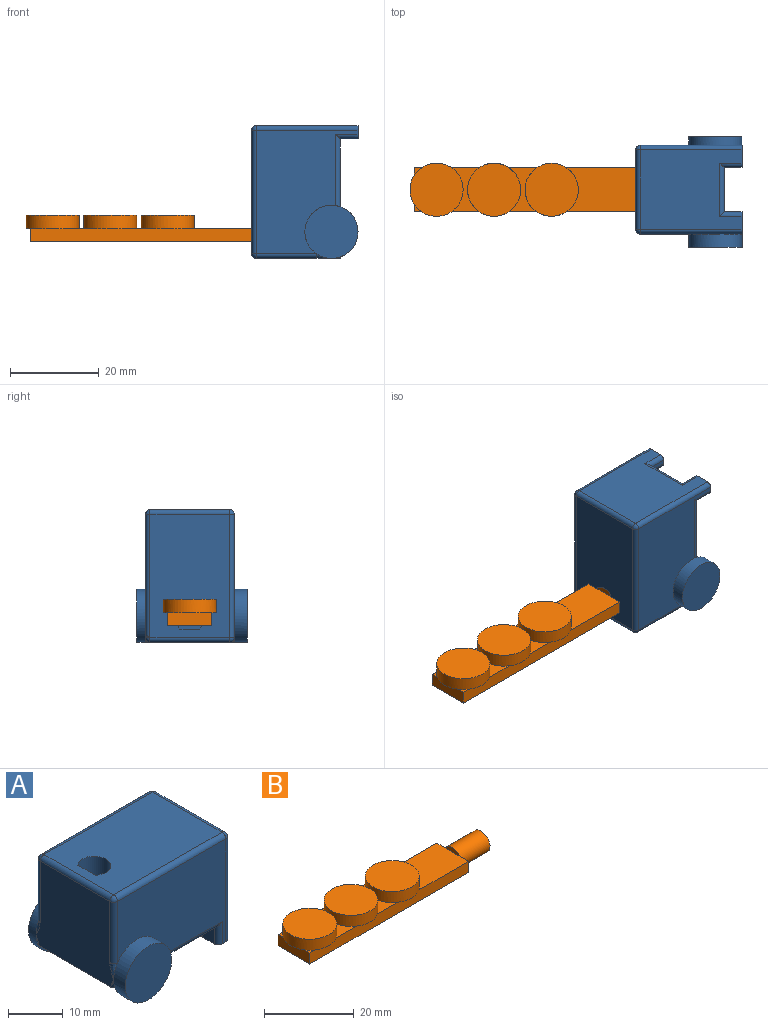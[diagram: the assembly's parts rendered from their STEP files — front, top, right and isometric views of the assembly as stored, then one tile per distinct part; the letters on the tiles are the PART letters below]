
ASSEMBLY  parts=2 mates=1
PART A: 46 faces, bbox 30.5x25.5x24.5 mm
  f0: plane 28x23mm, normal (0,-1,0), area 443.7mm2, adj f9,f20,f30,f31,f33,f36,f37
  f1: plane 28x18mm, normal (0,0,1), area 478.8mm2, adj f6,f7,f37,f38,f42,f43
  f2: plane 23x18mm, normal (1,0,0), area 354mm2, adj f17,f20,f23,f24,f25,f36,f42,f45
  f3: plane 28x23mm, normal (0,1,0), area 443.7mm2, adj f13,f17,f27,f28,f39,f43,f45
  f4: plane 20.48x19.48mm, normal (-1,0,0), area 346.8mm2, adj f5,f21,f22,f32,f33,f35,f38,f39
  f5: plane 29.06x20.06mm, normal (0,0,-1), area 529.6mm2, adj f4,f9,f11,f12,f13,f15,f16,f18
  f6: plane 10x4.47mm, normal (1,0,0), area 44.7mm2, adj f1,f7,f8
  f7: cylinder r=3mm len=10mm, axis (0,0,1), area 138mm2, adj f1,f6,f8
  f8: plane 6x5mm, normal (0,0,1), area 25.2mm2, adj f6,f7
  f9: cylinder r=6mm len=12mm, axis (0,1,0), area 113.6mm2, adj f0,f5,f10,f11,f22,f30,f32
  f10: plane 12x12mm, normal (0,-1,0), area 113.1mm2, adj f9
  f11: plane 11.31x4mm, normal (0,1,0), area 33mm2, adj f5,f9
  f12: plane 11.31x4mm, normal (0,-1,0), area 33mm2, adj f5,f13
  f13: cylinder r=6mm len=12mm, axis (0,-1,0), area 75.9mm2, adj f3,f5,f12,f14,f21,f27,f35
  f14: plane 12x12mm, normal (0,1,0), area 113.1mm2, adj f13
  f15: plane 4x1mm, normal (0,-1,0), area 4mm2, adj f5,f17,f25,f26
  f16: plane 4x3mm, normal (-1,0,0), area 12mm2, adj f5,f17,f26,f28
  f17: plane 5x3mm, normal (0,0,-1), area 14.1mm2, adj f2,f3,f15,f16,f25,f26,f28,f45
  f18: plane 4x3mm, normal (-1,0,0), area 12mm2, adj f5,f20,f29,f31
  f19: plane 4x1mm, normal (0,1,0), area 4mm2, adj f5,f20,f23,f29
  f20: plane 5x3mm, normal (0,0,-1), area 14.1mm2, adj f0,f2,f18,f19,f23,f29,f31,f36
  f21: bspline ~2.57x0.89mm, area 0.6mm2, adj f4,f5,f13
  f22: bspline ~2.57x0.89mm, area 0.6mm2, adj f4,f5,f9
  f23: cylinder r=1mm len=5mm, axis (0,0,1), area 7.1mm2, adj f2,f19,f20,f24
  f24: cylinder r=1mm len=12mm, axis (0,1,0), area 17.3mm2, adj f2,f5,f23,f25
  f25: cylinder r=1mm len=5mm, axis (0,0,-1), area 7.1mm2, adj f2,f15,f17,f24
  f26: cylinder r=1mm len=4mm, axis (0,0,-1), area 6.3mm2, adj f5,f15,f16,f17
  f27: cylinder r=1mm len=16.34mm, axis (-1,0,0), area 24.7mm2, adj f3,f5,f13,f28
  f28: cylinder r=1mm len=5mm, axis (0,0,-1), area 7.1mm2, adj f3,f16,f17,f27
  f29: cylinder r=1mm len=4mm, axis (0,0,-1), area 6.3mm2, adj f5,f18,f19,f20
  f30: cylinder r=1mm len=16.34mm, axis (1,0,0), area 24.7mm2, adj f0,f5,f9,f31
  f31: cylinder r=1mm len=5mm, axis (0,0,-1), area 7.1mm2, adj f0,f18,f20,f30
  f32: bspline ~3.69x1.19mm, area 1.6mm2, adj f4,f9,f33
  f33: cylinder r=1mm len=13.68mm, axis (0,0,1), area 21.5mm2, adj f0,f4,f32,f34
  f34: sphere r=1mm, area 1.6mm2, adj f33,f37,f38
  f35: bspline ~3.69x1.19mm, area 1.6mm2, adj f4,f13,f39
  f36: cylinder r=1mm len=23mm, axis (0,0,-1), area 36.1mm2, adj f0,f2,f20,f40
  f37: cylinder r=1mm len=28mm, axis (-1,0,0), area 44mm2, adj f0,f1,f34,f40
  f38: cylinder r=1mm len=18mm, axis (0,1,0), area 28.3mm2, adj f1,f4,f34,f41
  f39: cylinder r=1mm len=13.68mm, axis (0,0,-1), area 21.5mm2, adj f3,f4,f35,f41
  f40: sphere r=1mm, area 1.6mm2, adj f36,f37,f42
  f41: sphere r=1mm, area 2.1mm2, adj f38,f39,f43
  f42: cylinder r=1mm len=18mm, axis (0,-1,0), area 28.3mm2, adj f1,f2,f40,f44
  f43: cylinder r=1mm len=28mm, axis (1,0,0), area 44mm2, adj f1,f3,f41,f44
  f44: sphere r=1mm, area 1mm2, adj f42,f43,f45
  f45: cylinder r=1mm len=23mm, axis (0,0,1), area 36.1mm2, adj f2,f3,f17,f44
PART B: 27 faces, bbox 60x12x6 mm
  f0: plane 3x2.7mm, normal (1,0,0), area 7.2mm2, adj f2,f7,f10,f25
  f1: plane 10x6.37mm, normal (0,0,1), area 25.9mm2, adj f7,f9,f17,f21
  f2: plane 15.68x10mm, normal (0,0,1), area 138mm2, adj f0,f6,f7,f9,f21,f24
  f3: plane 10x6.37mm, normal (0,0,1), area 25.9mm2, adj f7,f9,f13,f17
  f4: plane 1.68x1.68mm, normal (0,0,1), area 1.2mm2, adj f7,f8,f13
  f5: plane 1.68x1.68mm, normal (0,0,1), area 1.2mm2, adj f8,f9,f13
  f6: plane 3x2.7mm, normal (1,0,0), area 7.2mm2, adj f2,f9,f10,f25
  f7: plane 50x3mm, normal (0,1,0), area 150mm2, adj f0,f1,f2,f3,f4,f8,f10,f11
  f8: plane 10x3mm, normal (-1,0,0), area 30mm2, adj f4,f5,f7,f9,f10,f12
  f9: plane 50x3mm, normal (0,-1,0), area 150mm2, adj f1,f2,f3,f5,f6,f8,f10,f15
  f10: plane 59x10mm, normal (0,0,-1), area 541.5mm2, adj f0,f6,f7,f8,f9,f25,f26
  f11: plane 6.63x1mm, normal (0,0,-1), area 4.5mm2, adj f7,f13
  f12: plane 6.63x1mm, normal (0,0,-1), area 4.5mm2, adj f8,f13
  f13: cylinder r=6mm len=12mm, axis (0,0,-1), area 113.1mm2, adj f3,f4,f5,f11,f12,f14,f15
  f14: plane 12x12mm, normal (0,0,1), area 113.1mm2, adj f13
  f15: plane 6.63x1mm, normal (0,0,-1), area 4.5mm2, adj f9,f13
  f16: plane 6.63x1mm, normal (0,0,-1), area 4.5mm2, adj f7,f17
  f17: cylinder r=6mm len=12mm, axis (0,0,-1), area 113.1mm2, adj f1,f3,f16,f18,f19
  f18: plane 12x12mm, normal (0,0,1), area 113.1mm2, adj f17
  f19: plane 6.63x1mm, normal (0,0,-1), area 4.5mm2, adj f9,f17
  f20: plane 6.63x1mm, normal (0,0,-1), area 4.5mm2, adj f7,f21
  f21: cylinder r=6mm len=12mm, axis (0,0,-1), area 113.1mm2, adj f1,f2,f20,f22,f23
  f22: plane 12x12mm, normal (0,0,1), area 113.1mm2, adj f21
  f23: plane 6.63x1mm, normal (0,0,-1), area 4.5mm2, adj f9,f21
  f24: plane 4.61x1.25mm, normal (-1,0,0), area 4.1mm2, adj f2,f25
  f25: cylinder r=2.75mm len=9mm, axis (-1,0,0), area 106.3mm2, adj f0,f6,f10,f24,f26
  f26: plane 5.5x4.25mm, normal (1,0,0), area 19.7mm2, adj f10,f25
PLACE A rot(axis=(0,-1,0),90deg) t=(40.36,11.04,25.37)mm
PLACE B t=(-4.64,11.04,14.11)mm
MATE fastened A.f1 <-> B.f25  axis (-1,0,0) through (20.36,11.04,15.61)mm
